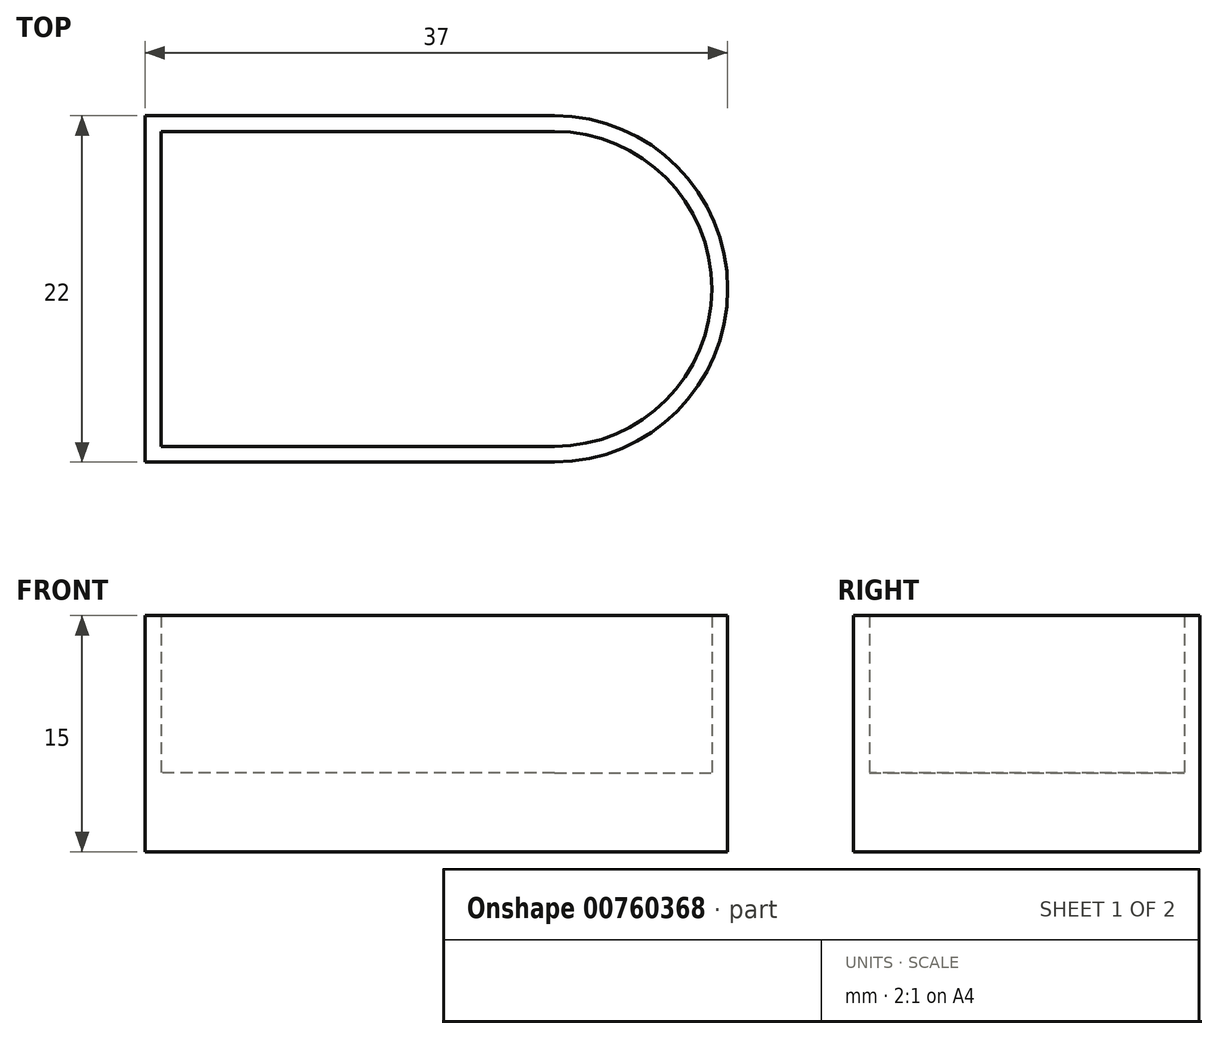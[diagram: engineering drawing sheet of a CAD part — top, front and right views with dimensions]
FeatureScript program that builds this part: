
annotation { "Feature Type Name" : "Feature", "Feature Type Description" : "" }
export const myFeature = defineFeature(function(context is Context, id is Id, definition is map)
    precondition{}
    {
        {
            var Q0;
            Q0=qCreatedBy(makeId("Top.planeOp"),FACE);
            var sketch = newSketch(context, id + "F0", { "sketchPlane" : qUnion([Q0])});
            skLineSegment(sketch, "E0.bottom", {"start": v(12.5, 10) * mm, "end": v(-12.5, 10) * mm});
            skLineSegment(sketch, "E0.top", {"start": v(12.5, -10) * mm, "end": v(-12.5, -10) * mm});
            skLineSegment(sketch, "E0.left", {"start": v(12.5, 10) * mm, "end": v(12.5, -10) * mm});
            skLineSegment(sketch, "E0.right", {"start": v(-12.5, 10) * mm, "end": v(-12.5, -10) * mm});
            skPoint(sketch, "E0.middle", {"position": v(0, 0) * mm});
            skArc(sketch, "E1", {"start": v(12.5, -10) * mm, "mid": v(22.5, 0) * mm, "end": v(12.5, 10) * mm});
            skLineSegment(sketch, "E2.0", {"start": v(12.5, 11) * mm, "end": v(-13.5, 11) * mm});
            skArc(sketch, "E2.1", {"start": v(12.5, -11) * mm, "mid": v(23.5, 0) * mm, "end": v(12.5, 11) * mm});
            skLineSegment(sketch, "E2.2", {"start": v(12.5, -11) * mm, "end": v(-13.5, -11) * mm});
            skLineSegment(sketch, "E2.3", {"start": v(-13.5, 11) * mm, "end": v(-13.5, -11) * mm});
            skSolve(sketch);
        }
        {
            var Q0;
            Q0=qSketchRegion(id+"F0",true);
            extrude(context, id + "F1", {"entities" : qUnion([Q0]), "depth" : 15 * mm});
        }
        {
            var Q0;
            Q0=makeQuery(id+"F0.imprint","IMPRINT",FACE,{"disambiguationData":[TD([[makeQuery(id+"F0.imprint","IMPRINT",EDGE,{"derivedFrom":sQuery(id+"F0.wireOp",EDGE,"E0.bottom")}),1.0]])]});
            var Q1;
            Q1=makeQuery(id+"F0.imprint","IMPRINT",FACE,{"disambiguationData":[TD([[makeQuery(id+"F0.imprint","IMPRINT",EDGE,{"derivedFrom":sQuery(id+"F0.wireOp",EDGE,"E0.left")}),1.0]])]});
            extrude(context, id + "F2", {"entities" : qUnion([Q0, Q1]), "operationType" : NewBodyOperationType.ADD, "depth" : 5 * mm});
        }
    });
